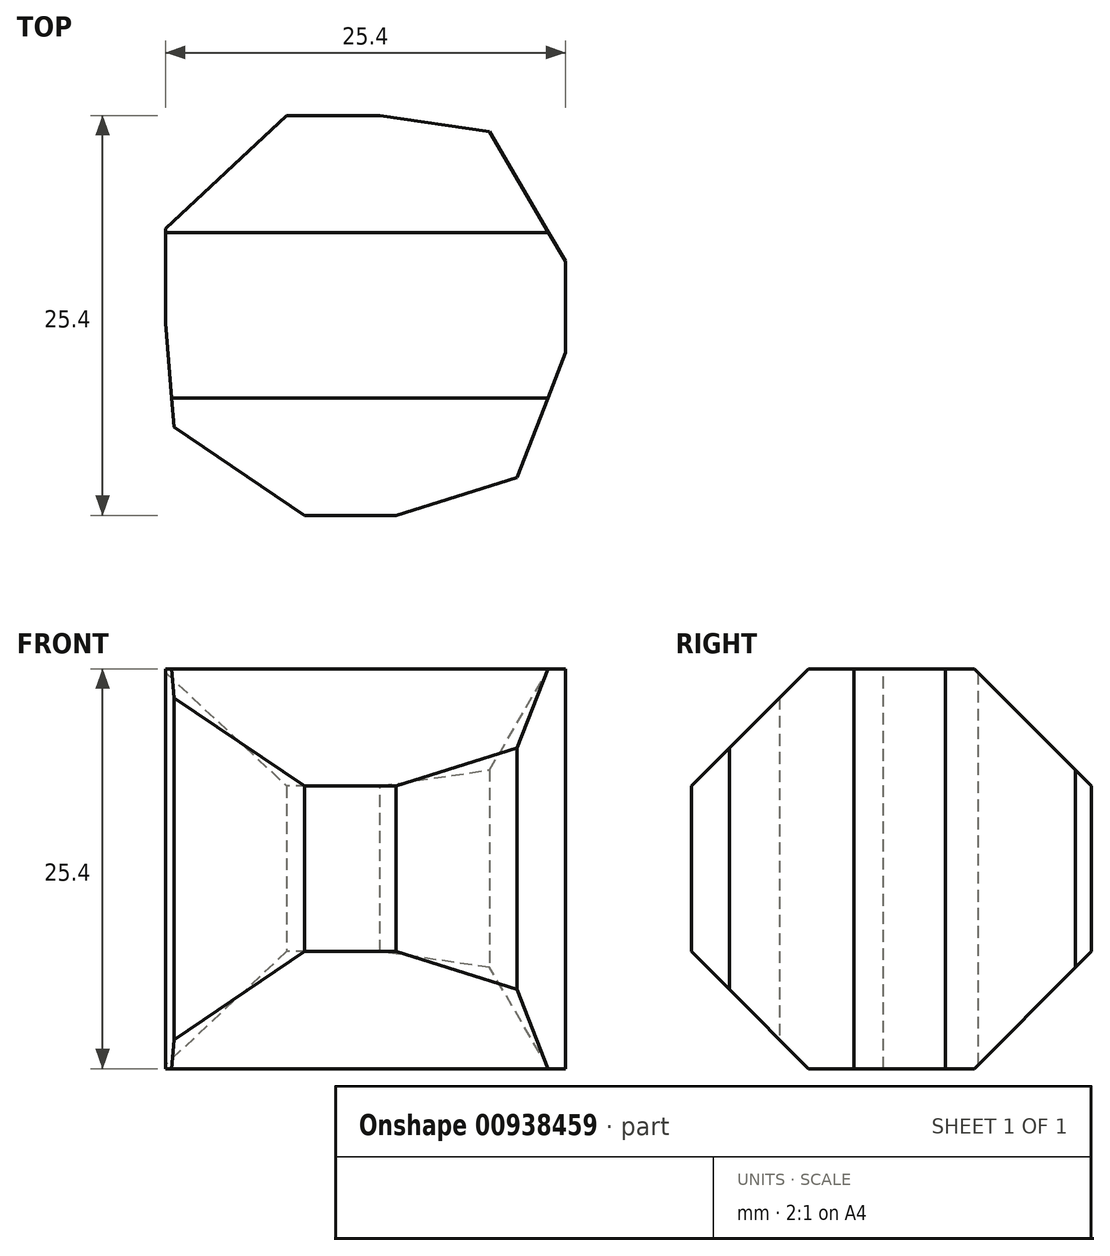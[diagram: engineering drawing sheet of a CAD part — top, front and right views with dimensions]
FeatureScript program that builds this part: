
annotation { "Feature Type Name" : "Feature", "Feature Type Description" : "" }
export const myFeature = defineFeature(function(context is Context, id is Id, definition is map)
    precondition{}
    {
        {
            var Q0;
            Q0=qCreatedBy(makeId("Top.planeOp"),FACE);
            var sketch = newSketch(context, id + "F0", { "sketchPlane" : qUnion([Q0])});
            skCircle(sketch, "E0.cCircle", {"center": v(0, 0) * mm, "radius": 12.7 * mm, "construction": true});
            skLineSegment(sketch, "E0.0", {"start": v(-4.21, 13.45) * mm, "end": v(7.89, 11.68) * mm});
            skLineSegment(sketch, "E0.1", {"start": v(7.89, 11.68) * mm, "end": v(14.05, 1.12) * mm});
            skLineSegment(sketch, "E0.2", {"start": v(14.05, 1.12) * mm, "end": v(9.63, -10.3) * mm});
            skLineSegment(sketch, "E0.3", {"start": v(9.63, -10.3) * mm, "end": v(-2.04, -13.95) * mm});
            skLineSegment(sketch, "E0.4", {"start": v(-2.04, -13.95) * mm, "end": v(-12.18, -7.1) * mm});
            skLineSegment(sketch, "E0.5", {"start": v(-12.18, -7.1) * mm, "end": v(-13.14, 5.1) * mm});
            skLineSegment(sketch, "E0.6", {"start": v(-13.14, 5.1) * mm, "end": v(-4.21, 13.45) * mm});
            skPoint(sketch, "E0.0.midPoint", {"position": v(1.84, 12.57) * mm});
            skSolve(sketch);
        }
        {
            var Q0;
            Q0=makeQuery(id+"F0.imprint","IMPRINT",FACE,{"disambiguationData":[TD([[makeQuery(id+"F0.imprint","IMPRINT",EDGE,{"derivedFrom":sQuery(id+"F0.wireOp",EDGE,"E0.0")}),-1.0]])]});
            extrude(context, id + "F1", {"entities" : qUnion([Q0]), "endBound" : BoundingType.SYMMETRIC, "depth" : 25.4 * mm, "offsetDistance" : 25.4 * mm});
        }
        {
            var Q0;
            Q0=qCreatedBy(makeId("Right.planeOp"),FACE);
            var sketch = newSketch(context, id + "F2", { "sketchPlane" : qUnion([Q0])});
            skCircle(sketch, "E1.cCircle", {"center": v(0, 0) * mm, "radius": 12.7 * mm, "construction": true});
            skLineSegment(sketch, "E1.0", {"start": v(-5.26, 12.7) * mm, "end": v(5.26, 12.7) * mm});
            skLineSegment(sketch, "E1.1", {"start": v(5.26, 12.7) * mm, "end": v(12.7, 5.26) * mm});
            skLineSegment(sketch, "E1.2", {"start": v(12.7, 5.26) * mm, "end": v(12.7, -5.26) * mm});
            skLineSegment(sketch, "E1.3", {"start": v(12.7, -5.26) * mm, "end": v(5.26, -12.7) * mm});
            skLineSegment(sketch, "E1.4", {"start": v(5.26, -12.7) * mm, "end": v(-5.26, -12.7) * mm});
            skLineSegment(sketch, "E1.5", {"start": v(-5.26, -12.7) * mm, "end": v(-12.7, -5.26) * mm});
            skLineSegment(sketch, "E1.6", {"start": v(-12.7, -5.26) * mm, "end": v(-12.7, 5.26) * mm});
            skLineSegment(sketch, "E1.7", {"start": v(-12.7, 5.26) * mm, "end": v(-5.26, 12.7) * mm});
            skPoint(sketch, "E1.0.midPoint", {"position": v(0, 12.7) * mm});
            skSolve(sketch);
        }
        {
            var Q0;
            Q0 = qSketchRegion(id + "F2", true);
            extrude(context, id + "F3", {"entities" : qUnion([Q0]), "operationType" : NewBodyOperationType.INTERSECT, "endBound" : BoundingType.SYMMETRIC, "depth" : 25.4 * mm, "offsetDistance" : 25.4 * mm});
        }
    });
